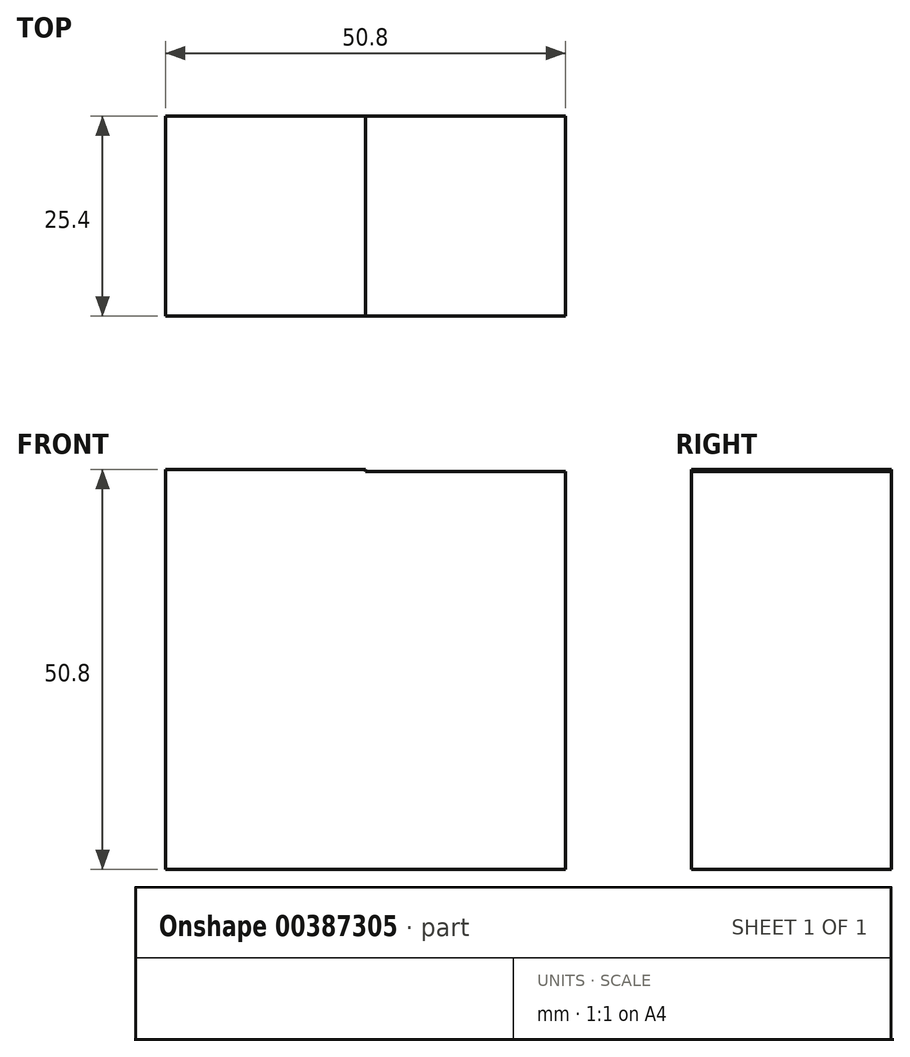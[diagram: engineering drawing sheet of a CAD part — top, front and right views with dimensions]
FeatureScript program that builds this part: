
annotation { "Feature Type Name" : "Feature", "Feature Type Description" : "" }
export const myFeature = defineFeature(function(context is Context, id is Id, definition is map)
    precondition{}
    {
        {
            var Q0;
            Q0=qCreatedBy(makeId("Front.planeOp"),FACE);
            var sketch = newSketch(context, id + "F0", { "sketchPlane" : qUnion([Q0])});
            skLineSegment(sketch, "E0.bottom", {"start": v(0, 0) * mm, "end": v(25.4, 0) * mm});
            skLineSegment(sketch, "E0.top", {"start": v(0, 25.17) * mm, "end": v(25.4, 25.17) * mm});
            skLineSegment(sketch, "E0.left", {"start": v(0, 0) * mm, "end": v(0, 25.17) * mm});
            skLineSegment(sketch, "E0.right", {"start": v(25.4, 0) * mm, "end": v(25.4, 25.17) * mm});
            skLineSegment(sketch, "E1.bottom", {"start": v(0, 0) * mm, "end": v(-25.4, 0) * mm});
            skLineSegment(sketch, "E1.top", {"start": v(0, 25.4) * mm, "end": v(-25.4, 25.4) * mm});
            skLineSegment(sketch, "E1.left", {"start": v(0, 0) * mm, "end": v(0, 25.4) * mm});
            skLineSegment(sketch, "E1.right", {"start": v(-25.4, 0) * mm, "end": v(-25.4, 25.4) * mm});
            skLineSegment(sketch, "E2.top", {"start": v(0, -25.4) * mm, "end": v(-25.4, -25.4) * mm});
            skLineSegment(sketch, "E2.left", {"start": v(0, 0) * mm, "end": v(0, -25.4) * mm});
            skLineSegment(sketch, "E2.right", {"start": v(-25.4, 0) * mm, "end": v(-25.4, -25.4) * mm});
            skLineSegment(sketch, "E3.top", {"start": v(0, -25.4) * mm, "end": v(25.4, -25.4) * mm});
            skLineSegment(sketch, "E3.right", {"start": v(25.4, 0) * mm, "end": v(25.4, -25.4) * mm});
            skSolve(sketch);
        }
        {
            var Q0;
            Q0 = qSketchRegion(id + "F0", true);
            extrude(context, id + "F1", {"entities" : qUnion([Q0]), "depth" : 25.4 * mm});
        }
    });
